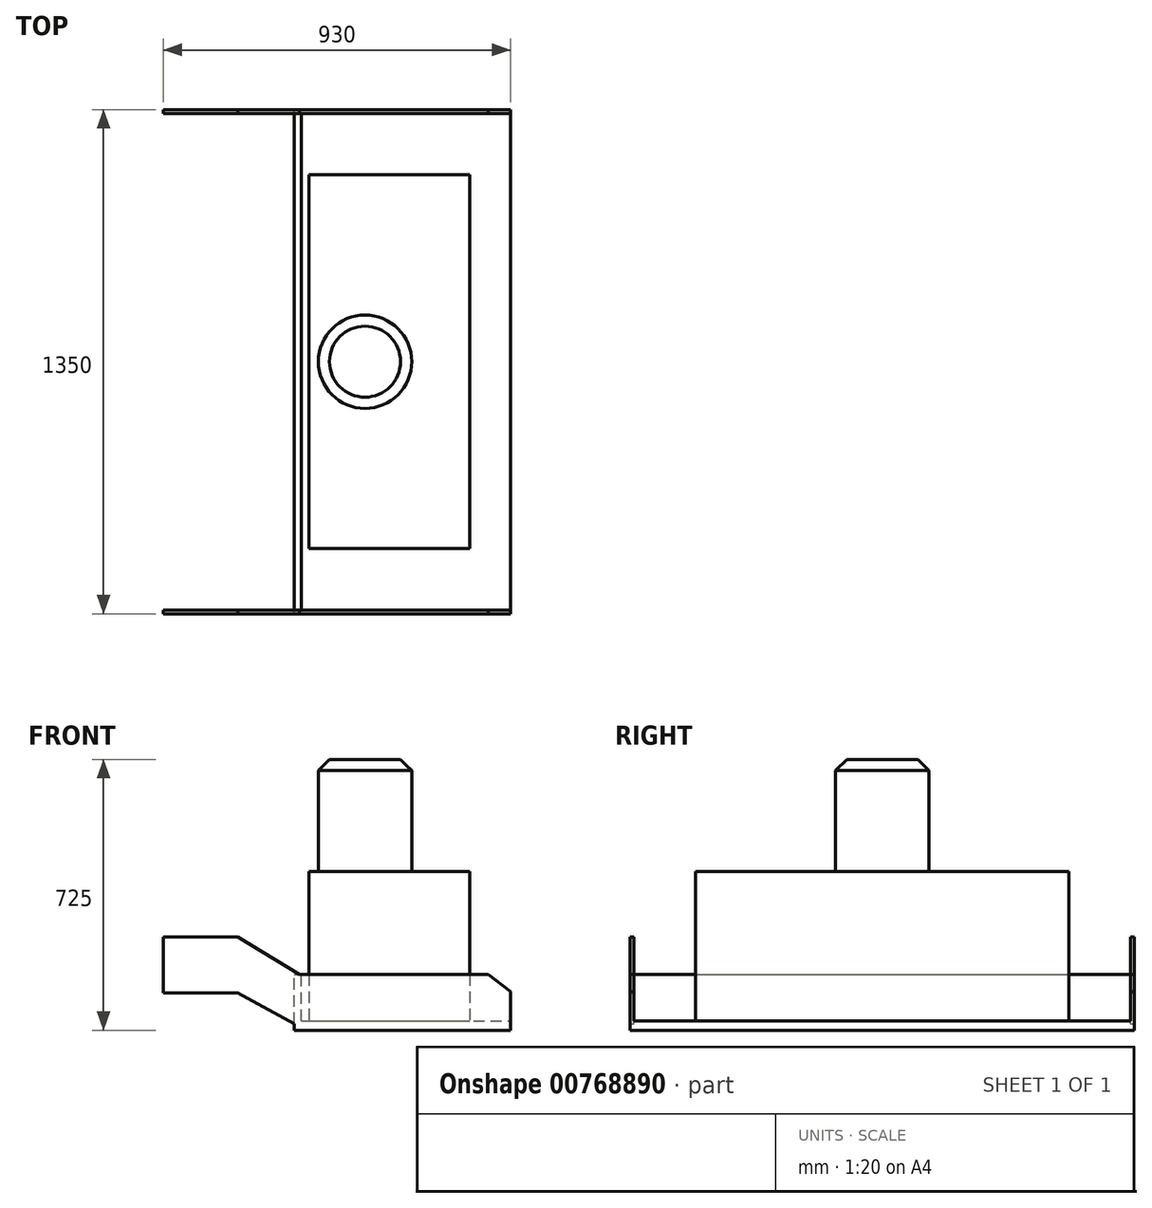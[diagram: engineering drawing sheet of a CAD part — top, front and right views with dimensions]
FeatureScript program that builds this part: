
annotation { "Feature Type Name" : "Feature", "Feature Type Description" : "" }
export const myFeature = defineFeature(function(context is Context, id is Id, definition is map)
    precondition{}
    {
        {
            var Q0;
            Q0=qCreatedBy(makeId("Front.planeOp"),FACE);
            var sketch = newSketch(context, id + "F0", { "sketchPlane" : qUnion([Q0])});
            skLineSegment(sketch, "E0.bottom", {"start": v(0, 250) * mm, "end": v(200, 250) * mm});
            skLineSegment(sketch, "E0.top", {"start": v(0, 100) * mm, "end": v(200, 100) * mm});
            skLineSegment(sketch, "E0.left", {"start": v(0, 250) * mm, "end": v(0, 100) * mm});
            skLineSegment(sketch, "E0.right", {"start": v(200, 250) * mm, "end": v(200, 100) * mm});
            skLineSegment(sketch, "E1.bottom", {"start": v(350, 0) * mm, "end": v(930, 0) * mm});
            skLineSegment(sketch, "E1.top", {"start": v(364.7, 150) * mm, "end": v(869.5, 150) * mm});
            skLineSegment(sketch, "E1.left", {"start": v(350, 0) * mm, "end": v(350, 17.27) * mm});
            skLineSegment(sketch, "E1.right", {"start": v(930, 0) * mm, "end": v(930, 103.2) * mm});
            skLineSegment(sketch, "E2", {"start": v(200, 100) * mm, "end": v(350, 17.27) * mm});
            skLineSegment(sketch, "E3", {"start": v(200, 250) * mm, "end": v(364.7, 150) * mm});
            skLineSegment(sketch, "E4", {"start": v(869.5, 150) * mm, "end": v(930, 103.2) * mm});
            skSolve(sketch);
        }
        {
            var Q0;
            Q0 = qSketchRegion(id + "F0", true);
            extrude(context, id + "F1", {"entities" : qUnion([Q0]), "depth" : 10 * mm, "offsetDistance" : 25 * mm});
        }
        {
            var Q0;
            Q0=makeQuery(id+"F1.opExtrude","CAP_FACE",FACE,{"disambiguationData":[OSD([sQuery(id+"F0.wireOp",EDGE,"E0.bottom"),sQuery(id+"F0.wireOp",EDGE,"E0.top"),sQuery(id+"F0.wireOp",EDGE,"E0.left"),sQuery(id+"F0.wireOp",EDGE,"E1.bottom"),sQuery(id+"F0.wireOp",EDGE,"E1.top"),sQuery(id+"F0.wireOp",EDGE,"E1.left"),sQuery(id+"F0.wireOp",EDGE,"E1.right"),sQuery(id+"F0.wireOp",EDGE,"E2"),sQuery(id+"F0.wireOp",EDGE,"E3"),sQuery(id+"F0.wireOp",EDGE,"E4")])],"isStart":false});
            var sketch = newSketch(context, id + "F2", { "sketchPlane" : qUnion([Q0])});
            skLineSegment(sketch, "E5.bottom", {"start": v(350, 0) * mm, "end": v(930, 0) * mm});
            skLineSegment(sketch, "E5.top", {"start": v(350, 25) * mm, "end": v(930, 25) * mm});
            skLineSegment(sketch, "E5.left", {"start": v(350, 0) * mm, "end": v(350, 25) * mm});
            skLineSegment(sketch, "E5.right", {"start": v(930, 0) * mm, "end": v(930, 25) * mm});
            skLineSegment(sketch, "E6.bottom", {"start": v(350, 25) * mm, "end": v(370, 25) * mm});
            skLineSegment(sketch, "E6.top", {"start": v(350, 150) * mm, "end": v(370, 150) * mm});
            skLineSegment(sketch, "E6.left", {"start": v(350, 25) * mm, "end": v(350, 150) * mm});
            skLineSegment(sketch, "E6.right", {"start": v(370, 25) * mm, "end": v(370, 150) * mm});
            skSolve(sketch);
        }
        {
            var Q0;
            Q0 = qSketchRegion(id + "F2", true);
            extrude(context, id + "F3", {"entities" : qUnion([Q0]), "operationType" : NewBodyOperationType.ADD, "depth" : 1330 * mm, "offsetDistance" : 25 * mm});
        }
        {
            var Q0;
            Q0=makeQuery(id+"F3.opExtrude","CAP_FACE",FACE,{"disambiguationData":[OSD([sQuery(id+"F2.wireOp",EDGE,"E5.bottom"),sQuery(id+"F2.wireOp",EDGE,"E5.top"),sQuery(id+"F2.wireOp",EDGE,"E5.left"),sQuery(id+"F2.wireOp",EDGE,"E5.right"),sQuery(id+"F2.wireOp",EDGE,"E6.top"),sQuery(id+"F2.wireOp",EDGE,"E6.left"),sQuery(id+"F2.wireOp",EDGE,"E6.right")])],"isStart":false});
            var sketch = newSketch(context, id + "F4", { "sketchPlane" : qUnion([Q0])});
            skPoint(sketch, "E7.0", {"position": v(0, 175) * mm});
            skLineSegment(sketch, "E8.0", {"start": v(0, 250) * mm, "end": v(0, 100) * mm});
            skLineSegment(sketch, "E9.0", {"start": v(0, 250) * mm, "end": v(200, 250) * mm});
            skLineSegment(sketch, "E10.0", {"start": v(200, 250) * mm, "end": v(364.7, 150) * mm});
            skLineSegment(sketch, "E11.0", {"start": v(0, 100) * mm, "end": v(200, 100) * mm});
            skLineSegment(sketch, "E12.0", {"start": v(200, 100) * mm, "end": v(350, 17.27) * mm});
            skLineSegment(sketch, "E13.0", {"start": v(370, 150) * mm, "end": v(869.5, 150) * mm});
            skPoint(sketch, "E14.0", {"position": v(899.75, 126.6) * mm});
            skLineSegment(sketch, "E15.0", {"start": v(869.5, 150) * mm, "end": v(930, 103.2) * mm});
            skLineSegment(sketch, "E16.0", {"start": v(930, 25) * mm, "end": v(930, 103.2) * mm});
            skLineSegment(sketch, "E17.0", {"start": v(930, 0) * mm, "end": v(930, 25) * mm});
            skLineSegment(sketch, "E18.0", {"start": v(350, 0) * mm, "end": v(930, 0) * mm});
            skLineSegment(sketch, "E19.0", {"start": v(350, 0) * mm, "end": v(350, 150) * mm});
            skSolve(sketch);
        }
        {
            var Q0;
            Q0=makeQuery(id+"F4.imprint","IMPRINT",FACE,{"disambiguationData":[TD([[makeQuery(id+"F4.imprint","IMPRINT",EDGE,{"derivedFrom":sQuery(id+"F4.wireOp",EDGE,"E8.0")}),1.0]])]});
            var Q1;
            Q1=makeQuery(id+"F4.imprint","IMPRINT",FACE,{"disambiguationData":[TD([[makeQuery(id+"F4.imprint","IMPRINT",EDGE,{"derivedFrom":sQuery(id+"F4.wireOp",EDGE,"E17.0")}),1.0]])]});
            var Q2;
            Q2=makeQuery(id+"F4.imprint","IMPRINT",FACE,{"disambiguationData":[TD([[makeQuery(id+"F4.imprint","IMPRINT",EDGE,{"derivedFrom":sQuery(id+"F4.wireOp",EDGE,"E13.0")}),-1.0]])]});
            extrude(context, id + "F5", {"entities" : qUnion([Q0, Q1, Q2]), "operationType" : NewBodyOperationType.ADD, "depth" : 10 * mm, "offsetDistance" : 25 * mm});
        }
        {
            var Q0;
            Q0=makeQuery(id+"F3.opExtrude","SWEPT_FACE",FACE,{"disambiguationData":[OSD([sQuery(id+"F2.wireOp",EDGE,"E5.top")])]});
            var sketch = newSketch(context, id + "F6", { "sketchPlane" : qUnion([Q0])});
            skLineSegment(sketch, "E20.bottom", {"start": v(390, -1175) * mm, "end": v(820, -1175) * mm});
            skLineSegment(sketch, "E20.top", {"start": v(390, -175) * mm, "end": v(820, -175) * mm});
            skLineSegment(sketch, "E20.left", {"start": v(390, -1175) * mm, "end": v(390, -175) * mm});
            skLineSegment(sketch, "E20.right", {"start": v(820, -1175) * mm, "end": v(820, -175) * mm});
            skSolve(sketch);
        }
        {
            var Q0;
            Q0=makeQuery(id+"F6.imprint","IMPRINT",FACE,{"disambiguationData":[TD([[makeQuery(id+"F6.imprint","IMPRINT",EDGE,{"derivedFrom":sQuery(id+"F6.wireOp",EDGE,"E20.bottom")}),1.0]])]});
            extrude(context, id + "F7", {"entities" : qUnion([Q0]), "depth" : 400 * mm, "offsetDistance" : 25 * mm});
        }
        {
            var Q0;
            Q0=makeQuery(id+"F7.opExtrude","CAP_FACE",FACE,{"disambiguationData":[OSD([sQuery(id+"F6.wireOp",EDGE,"E20.bottom"),sQuery(id+"F6.wireOp",EDGE,"E20.top"),sQuery(id+"F6.wireOp",EDGE,"E20.left"),sQuery(id+"F6.wireOp",EDGE,"E20.right")])],"isStart":false});
            var sketch = newSketch(context, id + "F8", { "sketchPlane" : qUnion([Q0])});
            skCircle(sketch, "E21", {"center": v(540, -675) * mm, "radius": 125 * mm});
            skSolve(sketch);
        }
        {
            var Q0;
            Q0=makeQuery(id+"F8.imprint","IMPRINT",FACE,{"disambiguationData":[TD([[makeQuery(id+"F8.imprint","IMPRINT",EDGE,{"derivedFrom":sQuery(id+"F8.wireOp",EDGE,"E21")}),1.0]])]});
            extrude(context, id + "F9", {"entities" : qUnion([Q0]), "operationType" : NewBodyOperationType.ADD, "depth" : 300 * mm, "offsetDistance" : 25 * mm});
        }
        {
            var Q0;
            Q0=makeQuery(id+"F9.opExtrude","CAP_EDGE",EDGE,{"disambiguationData":[OSD([sQuery(id+"F8.wireOp",EDGE,"E21")])],"isStart":false});
            chamfer(context, id + "F10", {"entities" : qUnion([Q0]), "width" : 30 * mm, "tangentPropagation" : true});
        }
    });
